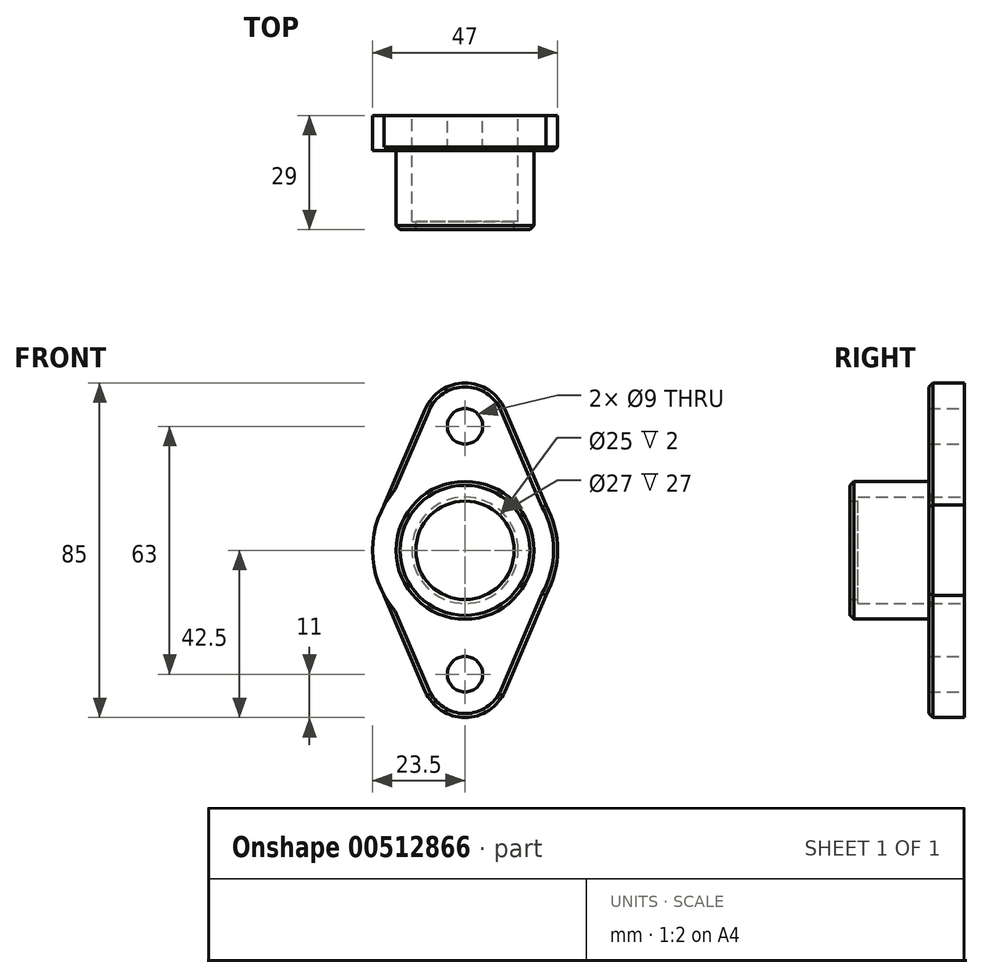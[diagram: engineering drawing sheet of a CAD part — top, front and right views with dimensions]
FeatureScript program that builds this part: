
annotation { "Feature Type Name" : "Feature", "Feature Type Description" : "" }
export const myFeature = defineFeature(function(context is Context, id is Id, definition is map)
    precondition{}
    {
        {
            var Q0;
            Q0=qCreatedBy(makeId("Front.planeOp"),FACE);
            var sketch = newSketch(context, id + "F0", { "sketchPlane" : qUnion([Q0])});
            skCircle(sketch, "E0", {"center": v(0, 0) * mm, "radius": 12.5 * mm});
            skCircle(sketch, "E1.0", {"center": v(0, 0) * mm, "radius": 17.5 * mm});
            skArc(sketch, "E2", {"start": v(20.52, -11.46) * mm, "mid": v(23.5, 0) * mm, "end": v(20.52, 11.46) * mm});
            skCircle(sketch, "E3", {"center": v(0, 31.5) * mm, "radius": 4.5 * mm});
            skArc(sketch, "E4", {"start": v(10.12, 35.82) * mm, "mid": v(0, 42.5) * mm, "end": v(-10.12, 35.82) * mm});
            skLineSegment(sketch, "E5", {"start": v(-5.25, 0) * mm, "end": v(6.08, 0) * mm, "construction": true});
            skArc(sketch, "E6.MirrorC", {"start": v(10.12, -35.82) * mm, "mid": v(0, -42.5) * mm, "end": v(-10.12, -35.82) * mm});
            skCircle(sketch, "E7.MirrorC", {"center": v(0, -31.5) * mm, "radius": 4.5 * mm});
            skLineSegment(sketch, "E8", {"start": v(-20.52, 11.46) * mm, "end": v(-10.12, 35.82) * mm});
            skLineSegment(sketch, "E9", {"start": v(0, -4.65) * mm, "end": v(0, 5.58) * mm, "construction": true});
            skLineSegment(sketch, "E10.MirrorCS", {"start": v(20.52, 11.46) * mm, "end": v(10.12, 35.82) * mm});
            skLineSegment(sketch, "E11.MirrorCS", {"start": v(-20.52, -11.46) * mm, "end": v(-10.12, -35.82) * mm});
            skLineSegment(sketch, "E12.MirrorCS", {"start": v(20.52, -11.46) * mm, "end": v(10.12, -35.82) * mm});
            skArc(sketch, "E13.trimOffspring", {"start": v(-20.52, 11.46) * mm, "mid": v(-23.5, 0) * mm, "end": v(-20.52, -11.46) * mm});
            skCircle(sketch, "E14.0", {"center": v(0, 0) * mm, "radius": 13.5 * mm});
            skSolve(sketch);
        }
        {
            var Q0;
            Q0 = qSketchRegion(id + "F0", true);
            extrude(context, id + "F1", {"entities" : qUnion([Q0]), "depth" : 9 * mm});
        }
        {
            var Q0;
            Q0=makeQuery(id+"F0.imprint","IMPRINT",FACE,{"disambiguationData":[TD([[makeQuery(id+"F0.imprint","IMPRINT",EDGE,{"derivedFrom":sQuery(id+"F0.wireOp",EDGE,"E1.0")}),1.0]])]});
            var Q1;
            Q1=makeQuery(id+"F0.imprint","IMPRINT",FACE,{"disambiguationData":[TD([[makeQuery(id+"F0.imprint","IMPRINT",EDGE,{"derivedFrom":sQuery(id+"F0.wireOp",EDGE,"E0")}),-1.0]])]});
            extrude(context, id + "F2", {"entities" : qUnion([Q0, Q1]), "operationType" : NewBodyOperationType.ADD, "depth" : 29 * mm});
        }
        {
            var Q0;
            Q0=makeQuery(id+"F0.imprint","IMPRINT",FACE,{"disambiguationData":[TD([[makeQuery(id+"F0.imprint","IMPRINT",EDGE,{"derivedFrom":sQuery(id+"F0.wireOp",EDGE,"E0")}),-1.0]])]});
            extrude(context, id + "F3", {"entities" : qUnion([Q0]), "operationType" : NewBodyOperationType.REMOVE, "depth" : 27 * mm});
        }
        {
            var Q0;
            Q0=makeQuery(id+"F2.opExtrude","CAP_EDGE",EDGE,{"disambiguationData":[OSD([sQuery(id+"F0.wireOp",EDGE,"E1.0")])],"isStart":false});
            var Q1;
            Q1=makeQuery(id+"F1.opExtrude","CAP_EDGE",EDGE,{"disambiguationData":[OSD([sQuery(id+"F0.wireOp",EDGE,"E2")])],"isStart":false});
            var Q2;
            Q2=makeQuery(id+"F1.opExtrude","CAP_EDGE",EDGE,{"disambiguationData":[OSD([sQuery(id+"F0.wireOp",EDGE,"E12.MirrorCS")])],"isStart":false});
            var Q3;
            Q3=makeQuery(id+"F1.opExtrude","CAP_EDGE",EDGE,{"disambiguationData":[OSD([sQuery(id+"F0.wireOp",EDGE,"E10.MirrorCS")])],"isStart":false});
            chamfer(context, id + "F4", {"entities" : qUnion([Q0, Q1, Q2, Q3]), "width" : 1 * mm, "tangentPropagation" : true});
        }
    });
